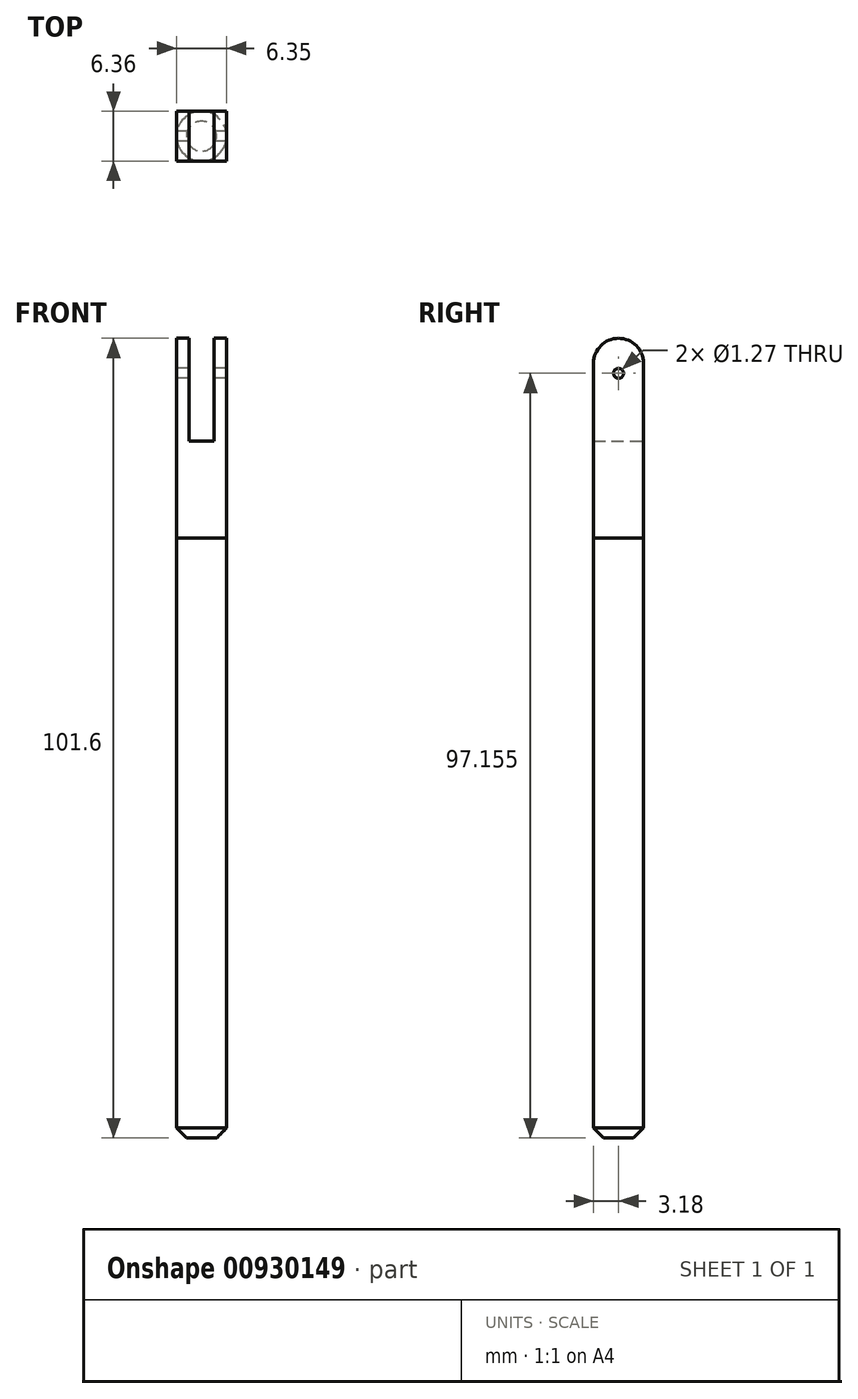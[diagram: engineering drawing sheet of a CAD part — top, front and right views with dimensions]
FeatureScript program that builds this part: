
annotation { "Feature Type Name" : "Feature", "Feature Type Description" : "" }
export const myFeature = defineFeature(function(context is Context, id is Id, definition is map)
    precondition{}
    {
        {
            var Q0;
            Q0=qCreatedBy(makeId("Front.planeOp"),FACE);
            var sketch = newSketch(context, id + "F0", { "sketchPlane" : qUnion([Q0])});
            skLineSegment(sketch, "E0.bottom", {"start": v(-3.76, 0) * mm, "end": v(2.59, 0) * mm});
            skLineSegment(sketch, "E0.top", {"start": v(-3.76, -76.2) * mm, "end": v(2.59, -76.2) * mm});
            skLineSegment(sketch, "E0.left", {"start": v(-3.76, 0) * mm, "end": v(-3.76, -76.2) * mm});
            skLineSegment(sketch, "E0.right", {"start": v(2.59, 0) * mm, "end": v(2.59, -76.2) * mm});
            skSolve(sketch);
        }
        {
            var Q0;
            Q0=qSketchRegion(id+"F0",true);
            extrude(context, id + "F1", {"entities" : qUnion([Q0]), "endBound" : BoundingType.SYMMETRIC, "depth" : 6.35 * mm, "offsetDistance" : 25.4 * mm});
        }
        {
            var Q0;
            Q0=makeQuery(id+"F1.opExtrude","CAP_EDGE",EDGE,{"disambiguationData":[OSD([sQuery(id+"F0.wireOp",EDGE,"E0.right")])],"isStart":false});
            var Q1;
            Q1=makeQuery(id+"F1.opExtrude","CAP_EDGE",EDGE,{"disambiguationData":[OSD([sQuery(id+"F0.wireOp",EDGE,"E0.right")])],"isStart":true});
            var Q2;
            Q2=makeQuery(id+"F1.opExtrude","CAP_EDGE",EDGE,{"disambiguationData":[OSD([sQuery(id+"F0.wireOp",EDGE,"E0.left")])],"isStart":false});
            var Q3;
            Q3=makeQuery(id+"F1.opExtrude","CAP_EDGE",EDGE,{"disambiguationData":[OSD([sQuery(id+"F0.wireOp",EDGE,"E0.left")])],"isStart":true});
            fillet(context, id + "F2", {"entities" : qUnion([Q0, Q1, Q2, Q3]), "radius" : 3.17 * mm, "tangentPropagation" : true, "allowEdgeOverflow" : false});
        }
        {
            var Q0;
            Q0=qCreatedBy(makeId("Front.planeOp"),FACE);
            var sketch = newSketch(context, id + "F3", { "sketchPlane" : qUnion([Q0])});
            skLineSegment(sketch, "E1.bottom", {"start": v(-3.76, 25.4) * mm, "end": v(2.59, 25.4) * mm});
            skLineSegment(sketch, "E1.top", {"start": v(-3.76, 0) * mm, "end": v(2.59, 0) * mm});
            skLineSegment(sketch, "E1.left", {"start": v(-3.76, 25.4) * mm, "end": v(-3.76, 0) * mm});
            skLineSegment(sketch, "E1.right", {"start": v(2.59, 25.4) * mm, "end": v(2.59, 0) * mm});
            skSolve(sketch);
        }
        {
            var Q0;
            Q0=qCreatedBy(makeId("Front.planeOp"),FACE);
            var sketch = newSketch(context, id + "F4", { "sketchPlane" : qUnion([Q0])});
            skLineSegment(sketch, "E2.bottom", {"start": v(1, 25.4) * mm, "end": v(-2.17, 25.4) * mm});
            skLineSegment(sketch, "E2.top", {"start": v(1, 12.33) * mm, "end": v(-2.17, 12.33) * mm});
            skLineSegment(sketch, "E2.left", {"start": v(1, 25.4) * mm, "end": v(1, 12.33) * mm});
            skLineSegment(sketch, "E2.right", {"start": v(-2.17, 25.4) * mm, "end": v(-2.17, 12.33) * mm});
            skSolve(sketch);
        }
        {
            var Q0;
            Q0=qSketchRegion(id+"F3",true);
            extrude(context, id + "F5", {"entities" : qUnion([Q0]), "operationType" : NewBodyOperationType.ADD, "endBound" : BoundingType.SYMMETRIC, "depth" : 6.35 * mm, "offsetDistance" : 25.4 * mm});
        }
        {
            var Q0;
            Q0=qSketchRegion(id+"F4",true);
            extrude(context, id + "F6", {"entities" : qUnion([Q0]), "operationType" : NewBodyOperationType.REMOVE, "endBound" : BoundingType.SYMMETRIC, "depth" : 10.16 * mm, "offsetDistance" : 25.4 * mm});
        }
        {
            var Q0;
            Q0=qCreatedBy(makeId("Right.planeOp"),FACE);
            var sketch = newSketch(context, id + "F7", { "sketchPlane" : qUnion([Q0])});
            skCircle(sketch, "E3", {"center": v(0, 20.96) * mm, "radius": 0.64 * mm});
            skSolve(sketch);
        }
        {
            var Q0;
            Q0=qSketchRegion(id+"F7",true);
            extrude(context, id + "F8", {"entities" : qUnion([Q0]), "operationType" : NewBodyOperationType.REMOVE, "endBound" : BoundingType.SYMMETRIC, "depth" : 7.62 * mm, "offsetDistance" : 25.4 * mm});
        }
        {
            var Q0;
            {var subQ0=sQuery(id+"F3.wireOp",EDGE,"E1.bottom");var subQ1=sQuery(id+"F3.wireOp",EDGE,"E1.left");Q0=makeQuery(id+"F6.boolean.opBoolean","SPLIT",EDGE,{"disambiguationData":[TD([makeQuery(id+"F5.opExtrude","SWEPT_FACE",FACE,{"disambiguationData":[OSD([subQ1])]})])],"derivedFrom":makeQuery(id+"F5.opExtrude","CAP_EDGE",EDGE,{"disambiguationData":[OSD([subQ0])],"isStart":false})});}
            var Q1;
            {var subQ0=sQuery(id+"F3.wireOp",EDGE,"E1.bottom");var subQ1=sQuery(id+"F3.wireOp",EDGE,"E1.right");Q1=makeQuery(id+"F6.boolean.opBoolean","SPLIT",EDGE,{"disambiguationData":[TD([makeQuery(id+"F5.opExtrude","SWEPT_FACE",FACE,{"disambiguationData":[OSD([subQ1])]})])],"derivedFrom":makeQuery(id+"F5.opExtrude","CAP_EDGE",EDGE,{"disambiguationData":[OSD([subQ0])],"isStart":false})});}
            var Q2;
            {var subQ0=sQuery(id+"F3.wireOp",EDGE,"E1.bottom");var subQ1=sQuery(id+"F3.wireOp",EDGE,"E1.right");Q2=makeQuery(id+"F6.boolean.opBoolean","SPLIT",EDGE,{"disambiguationData":[TD([makeQuery(id+"F5.opExtrude","SWEPT_FACE",FACE,{"disambiguationData":[OSD([subQ1])]})])],"derivedFrom":makeQuery(id+"F5.opExtrude","CAP_EDGE",EDGE,{"disambiguationData":[OSD([subQ0])],"isStart":true})});}
            var Q3;
            {var subQ0=sQuery(id+"F3.wireOp",EDGE,"E1.bottom");var subQ1=sQuery(id+"F3.wireOp",EDGE,"E1.left");Q3=makeQuery(id+"F6.boolean.opBoolean","SPLIT",EDGE,{"disambiguationData":[TD([makeQuery(id+"F5.opExtrude","SWEPT_FACE",FACE,{"disambiguationData":[OSD([subQ1])]})])],"derivedFrom":makeQuery(id+"F5.opExtrude","CAP_EDGE",EDGE,{"disambiguationData":[OSD([subQ0])],"isStart":true})});}
            fillet(context, id + "F9", {"entities" : qUnion([Q0, Q1, Q2, Q3]), "radius" : 3.17 * mm, "tangentPropagation" : true, "allowEdgeOverflow" : false});
        }
        {
            var Q0;
            Q0=makeQuery(id+"F2.opFillet","BLEND_EDGE",EDGE,{"blendedFrom":[makeQuery(id+"F1.opExtrude","CAP_EDGE",EDGE,{"disambiguationData":[OSD([sQuery(id+"F0.wireOp",EDGE,"E0.left")])],"isStart":true}),makeQuery(id+"F1.opExtrude","SWEPT_FACE",FACE,{"disambiguationData":[OSD([sQuery(id+"F0.wireOp",EDGE,"E0.top")])]})],"blendedInto":[makeQuery(id+"F1.opExtrude","SWEPT_FACE",FACE,{"disambiguationData":[OSD([sQuery(id+"F0.wireOp",EDGE,"E0.top")])]})]});
            chamfer(context, id + "F10", {"entities" : qUnion([Q0]), "width" : 1.27 * mm, "tangentPropagation" : true});
        }
    });
